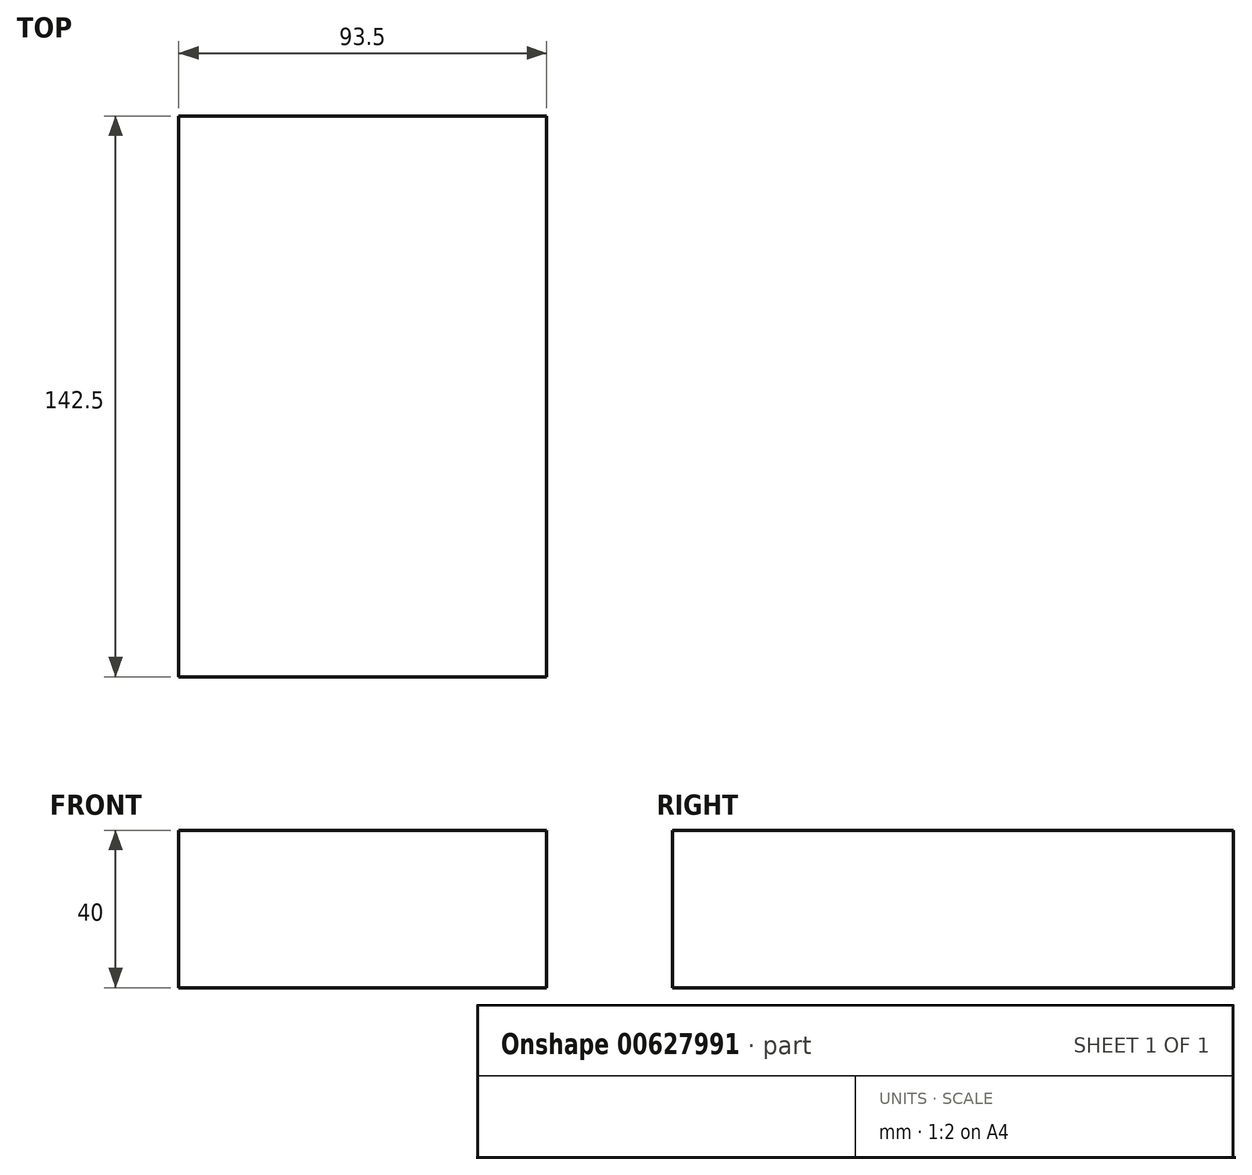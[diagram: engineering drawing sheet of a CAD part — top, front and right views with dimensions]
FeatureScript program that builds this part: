
annotation { "Feature Type Name" : "Feature", "Feature Type Description" : "" }
export const myFeature = defineFeature(function(context is Context, id is Id, definition is map)
    precondition{}
    {
        {
            var Q0;
            Q0=qCreatedBy(makeId("Top.planeOp"),FACE);
            var sketch = newSketch(context, id + "F0", { "sketchPlane" : qUnion([Q0])});
            skLineSegment(sketch, "E0.bottom", {"start": v(0, 0) * mm, "end": v(93.5, 0) * mm});
            skLineSegment(sketch, "E0.top", {"start": v(0, 142.5) * mm, "end": v(93.5, 142.5) * mm});
            skLineSegment(sketch, "E0.left", {"start": v(0, 0) * mm, "end": v(0, 142.5) * mm});
            skLineSegment(sketch, "E0.right", {"start": v(93.5, 0) * mm, "end": v(93.5, 142.5) * mm});
            skSolve(sketch);
        }
        {
            var Q0;
            Q0 = qSketchRegion(id + "F0", true);
            extrude(context, id + "F1", {"entities" : qUnion([Q0]), "depth" : 40 * mm, "offsetDistance" : 25 * mm});
        }
    });
